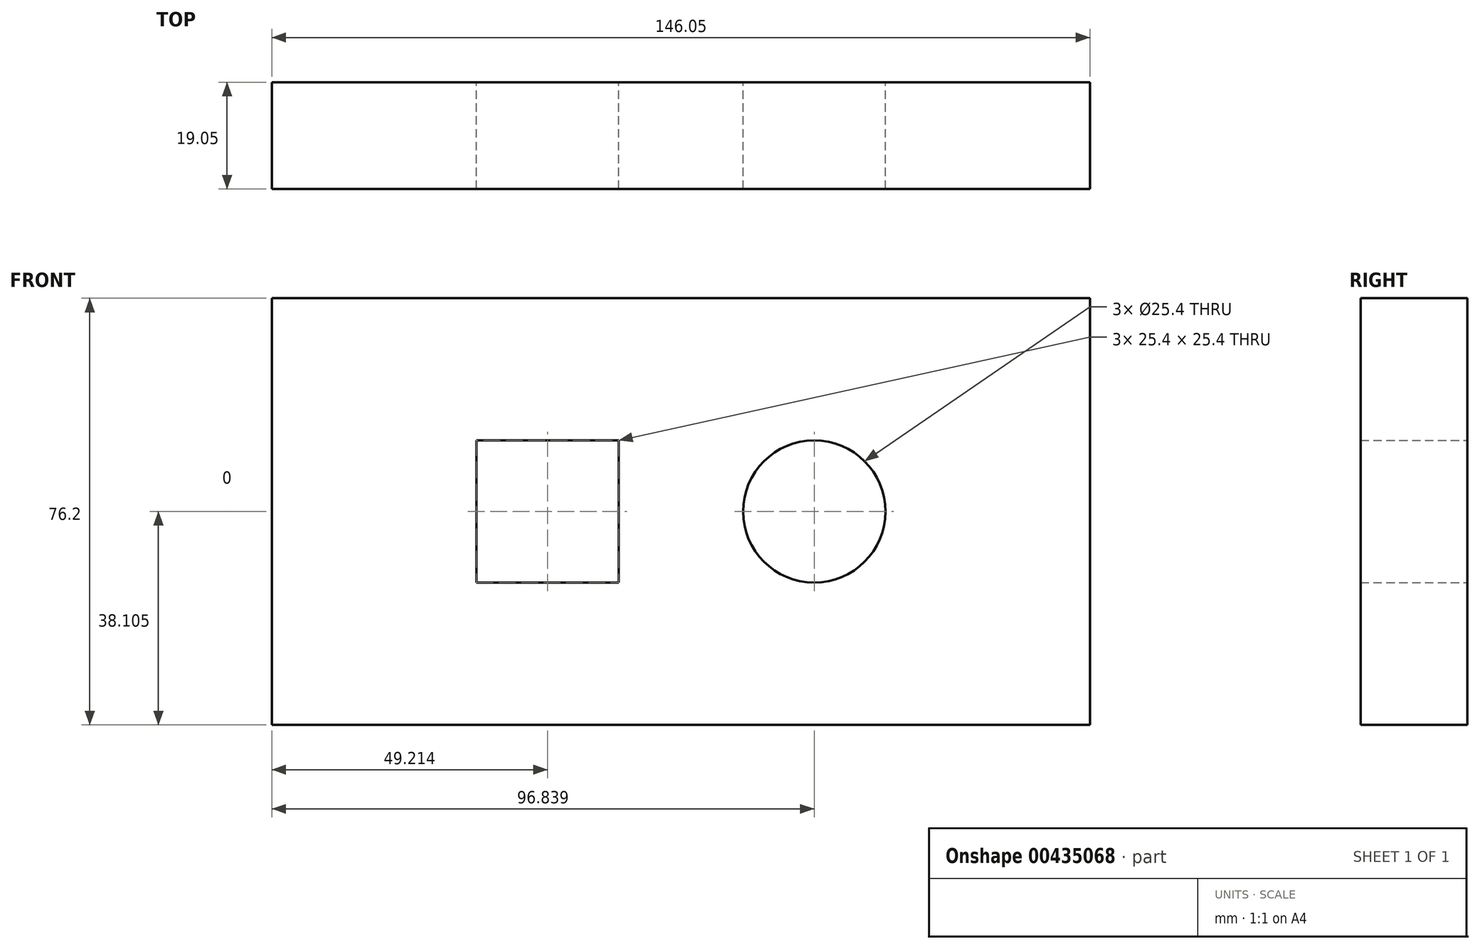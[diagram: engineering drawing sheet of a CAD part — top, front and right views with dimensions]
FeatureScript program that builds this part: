
annotation { "Feature Type Name" : "Feature", "Feature Type Description" : "" }
export const myFeature = defineFeature(function(context is Context, id is Id, definition is map)
    precondition{}
    {
        {
            var Q0;
            Q0=qCreatedBy(makeId("Front.planeOp"),FACE);
            var sketch = newSketch(context, id + "F0", { "sketchPlane" : qUnion([Q0])});
            skLineSegment(sketch, "E0.bottom", {"start": v(-93.17, 49.46) * mm, "end": v(52.88, 49.46) * mm});
            skLineSegment(sketch, "E0.top", {"start": v(-93.17, -26.74) * mm, "end": v(52.88, -26.74) * mm});
            skLineSegment(sketch, "E0.left", {"start": v(-93.17, 49.46) * mm, "end": v(-93.17, -26.74) * mm});
            skLineSegment(sketch, "E0.right", {"start": v(52.88, 49.46) * mm, "end": v(52.88, -26.74) * mm});
            skSolve(sketch);
        }
        {
            var Q0;
            Q0=makeQuery(id+"F0.imprint","IMPRINT",FACE,{"disambiguationData":[TD([[makeQuery(id+"F0.imprint","IMPRINT",EDGE,{"derivedFrom":sQuery(id+"F0.wireOp",EDGE,"E0.bottom")}),-1.0]])]});
            var sketch = newSketch(context, id + "F1", { "sketchPlane" : qUnion([Q0])});
            skCircle(sketch, "E1", {"center": v(3.67, 11.36) * mm, "radius": 12.7 * mm});
            skLineSegment(sketch, "E2.bottom", {"start": v(-56.66, 24.06) * mm, "end": v(-31.26, 24.06) * mm});
            skLineSegment(sketch, "E2.top", {"start": v(-56.66, -1.34) * mm, "end": v(-31.26, -1.34) * mm});
            skLineSegment(sketch, "E2.left", {"start": v(-56.66, 24.06) * mm, "end": v(-56.66, -1.34) * mm});
            skLineSegment(sketch, "E2.right", {"start": v(-31.26, 24.06) * mm, "end": v(-31.26, -1.34) * mm});
            skSolve(sketch);
        }
        {
            var Q0;
            Q0 = qSketchRegion(id + "F0", true);
            extrude(context, id + "F2", {"entities" : qUnion([Q0]), "depth" : 19.05 * mm});
        }
        {
            var Q0;
            Q0 = qSketchRegion(id + "F1", true);
            extrude(context, id + "F3", {"entities" : qUnion([Q0]), "operationType" : NewBodyOperationType.REMOVE, "depth" : 25.4 * mm});
        }
    });
